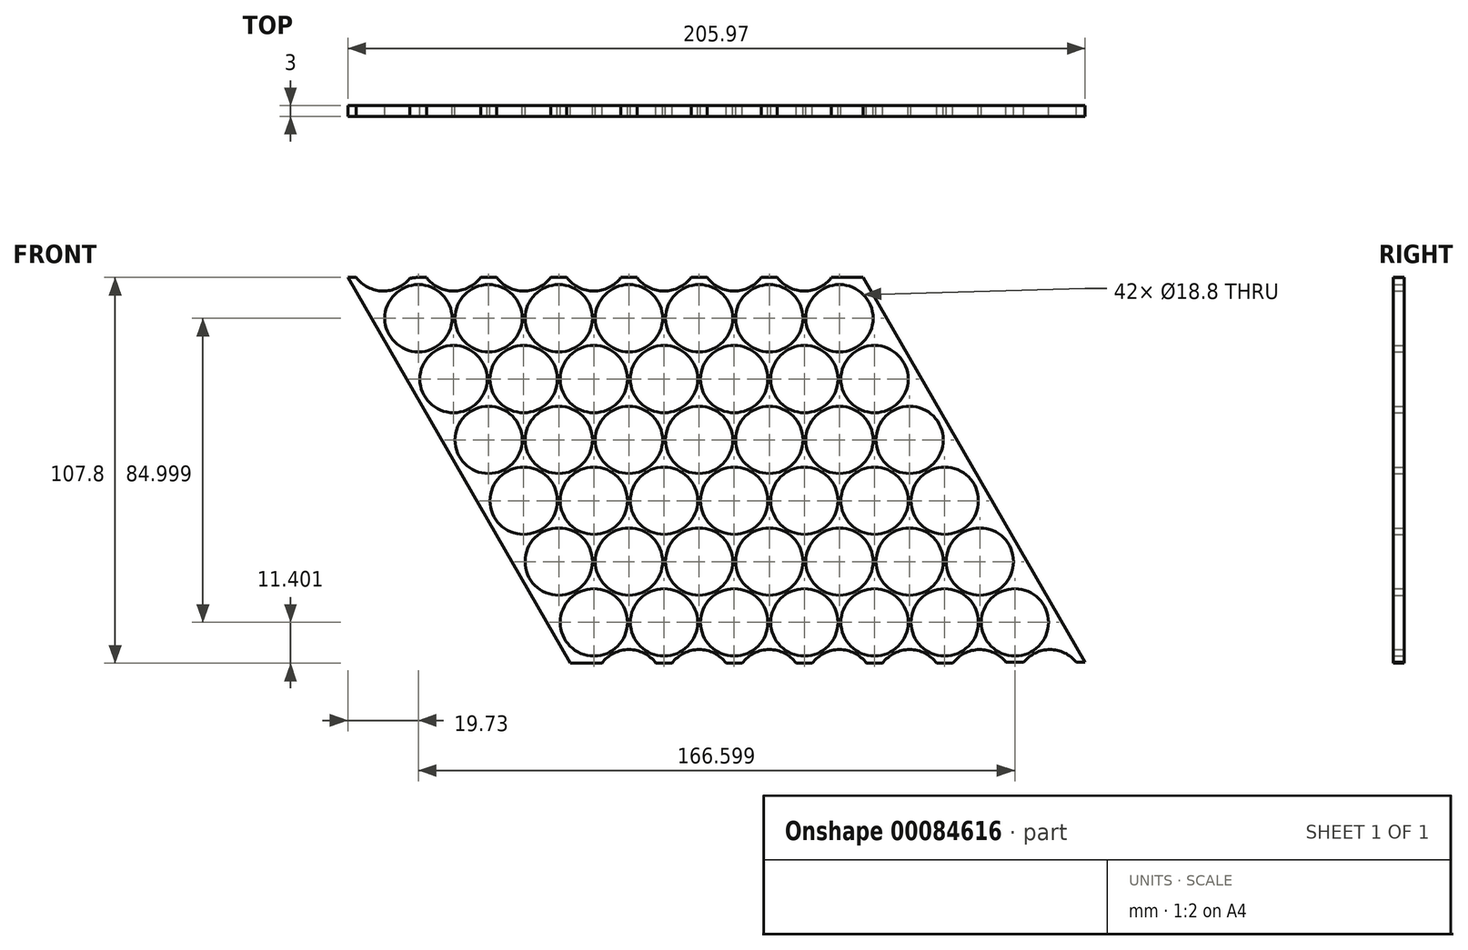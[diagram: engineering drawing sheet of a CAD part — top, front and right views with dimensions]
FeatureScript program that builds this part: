
annotation { "Feature Type Name" : "Feature", "Feature Type Description" : "" }
export const myFeature = defineFeature(function(context is Context, id is Id, definition is map)
    precondition{}
    {
        {
            var Q0;
            Q0=qCreatedBy(makeId("Front.planeOp"),FACE);
            var sketch = newSketch(context, id + "F0", { "sketchPlane" : qUnion([Q0])});
            skCircle(sketch, "E0", {"center": v(0, 0) * mm, "radius": 9.4 * mm});
            skCircle(sketch, "E1.1.0.0", {"center": v(19.6, 0) * mm, "radius": 9.4 * mm});
            skCircle(sketch, "E1.2.0.0", {"center": v(39.2, 0) * mm, "radius": 9.4 * mm});
            skCircle(sketch, "E1.3.0.0", {"center": v(58.8, 0) * mm, "radius": 9.4 * mm});
            skLineSegment(sketch, "E1.direction1", {"start": v(0, 0) * mm, "end": v(19.6, 0) * mm, "construction": true});
            skLineSegment(sketch, "E2", {"start": v(0, -17) * mm, "end": v(73.2, -17) * mm, "construction": true});
            skLineSegment(sketch, "E3", {"start": v(9.8, 0) * mm, "end": v(9.8, -17) * mm, "construction": true});
            skCircle(sketch, "E4", {"center": v(9.8, -17) * mm, "radius": 9.4 * mm});
            skCircle(sketch, "E5.1.0.0", {"center": v(29.4, -17) * mm, "radius": 9.4 * mm});
            skCircle(sketch, "E5.2.0.0", {"center": v(49, -17) * mm, "radius": 9.4 * mm});
            skCircle(sketch, "E5.3.0.0", {"center": v(68.6, -17) * mm, "radius": 9.4 * mm});
            skLineSegment(sketch, "E5.direction1", {"start": v(9.8, -17) * mm, "end": v(29.4, -17) * mm, "construction": true});
            skLineSegment(sketch, "E6", {"start": v(9.8, -17) * mm, "end": v(9.8, -26.4) * mm, "construction": true});
            skLineSegment(sketch, "E7", {"start": v(68.6, -17) * mm, "end": v(68.6, -26.4) * mm, "construction": true});
            skArc(sketch, "E8", {"start": v(58.8, 9.4) * mm, "mid": v(63.5, 8.14) * mm, "end": v(66.94, 4.7) * mm});
            skArc(sketch, "E9", {"start": v(76.74, -12.3) * mm, "mid": v(76.74, -21.7) * mm, "end": v(68.6, -26.4) * mm});
            skArc(sketch, "E10", {"start": v(9.8, -26.4) * mm, "mid": v(5.1, -25.14) * mm, "end": v(1.66, -21.7) * mm});
            skArc(sketch, "E11", {"start": v(-8.14, -4.7) * mm, "mid": v(-8.14, 4.7) * mm, "end": v(0, 9.4) * mm});
            skArc(sketch, "E12.0", {"start": v(0, 11.4) * mm, "mid": v(-1.24, 11.33) * mm, "end": v(-2.46, 11.13) * mm});
            skLineSegment(sketch, "E13.0", {"start": v(0, 11.4) * mm, "end": v(2.25, 11.4) * mm});
            skLineSegment(sketch, "E14.0", {"start": v(-9.88, -5.7) * mm, "end": v(-0.08, -22.7) * mm});
            skArc(sketch, "E15.trimOffspring", {"start": v(9.8, -5.82) * mm, "mid": v(9.87, -5.71) * mm, "end": v(9.93, -5.6) * mm});
            skArc(sketch, "E16.trimOffspring", {"start": v(9.93, -5.6) * mm, "mid": v(9.86, -5.6) * mm, "end": v(9.8, -5.6) * mm});
            skCircle(sketch, "E17.0.4.0", {"center": v(78.4, 0) * mm, "radius": 9.4 * mm});
            skCircle(sketch, "E17.0.5.0", {"center": v(98, 0) * mm, "radius": 9.4 * mm});
            skCircle(sketch, "E18.0.4.0", {"center": v(88.2, -17) * mm, "radius": 9.4 * mm});
            skCircle(sketch, "E18.0.5.0", {"center": v(107.8, -17) * mm, "radius": 9.4 * mm});
            skLineSegment(sketch, "E19", {"start": v(58.8, 11.4) * mm, "end": v(61.05, 11.4) * mm});
            skLineSegment(sketch, "E20", {"start": v(0, 0) * mm, "end": v(9.8, -17) * mm, "construction": true});
            skCircle(sketch, "E21.1.0.0", {"center": v(19.6, -34) * mm, "radius": 9.4 * mm});
            skCircle(sketch, "E21.2.0.0", {"center": v(29.4, -51) * mm, "radius": 9.4 * mm});
            skLineSegment(sketch, "E21.direction1", {"start": v(9.8, -17) * mm, "end": v(19.6, -34) * mm, "construction": true});
            skCircle(sketch, "E22.1.0.0", {"center": v(39.2, -34) * mm, "radius": 9.4 * mm});
            skCircle(sketch, "E22.1.0.1", {"center": v(49, -51) * mm, "radius": 9.4 * mm});
            skCircle(sketch, "E22.2.0.0", {"center": v(58.8, -34) * mm, "radius": 9.4 * mm});
            skCircle(sketch, "E22.2.0.1", {"center": v(68.6, -51) * mm, "radius": 9.4 * mm});
            skCircle(sketch, "E22.3.0.0", {"center": v(78.4, -34) * mm, "radius": 9.4 * mm});
            skCircle(sketch, "E22.3.0.1", {"center": v(88.2, -51) * mm, "radius": 9.4 * mm});
            skCircle(sketch, "E22.4.0.0", {"center": v(98, -34) * mm, "radius": 9.4 * mm});
            skCircle(sketch, "E22.4.0.1", {"center": v(107.8, -51) * mm, "radius": 9.4 * mm});
            skCircle(sketch, "E22.5.0.0", {"center": v(117.6, -34) * mm, "radius": 9.4 * mm});
            skCircle(sketch, "E22.5.0.1", {"center": v(127.4, -51) * mm, "radius": 9.4 * mm});
            skLineSegment(sketch, "E22.direction1", {"start": v(19.6, -34) * mm, "end": v(39.2, -34) * mm, "construction": true});
            skLineSegment(sketch, "E23", {"start": v(-0.08, -22.7) * mm, "end": v(19.52, -56.7) * mm});
            skArc(sketch, "E24.0", {"start": v(29.27, -62.4) * mm, "mid": v(29.33, -62.4) * mm, "end": v(29.4, -62.4) * mm});
            skCircle(sketch, "E25.0.6.0", {"center": v(117.6, 0) * mm, "radius": 9.4 * mm});
            skCircle(sketch, "E26.0.6.0", {"center": v(127.4, -17) * mm, "radius": 9.4 * mm});
            skCircle(sketch, "E27.0.6.0", {"center": v(137.2, -34) * mm, "radius": 9.4 * mm});
            skCircle(sketch, "E27.2.6.0", {"center": v(147, -51) * mm, "radius": 9.4 * mm});
            skLineSegment(sketch, "E28", {"start": v(98, 11.4) * mm, "end": v(100.25, 11.4) * mm});
            skCircle(sketch, "E29.0.3.0", {"center": v(39.2, -68) * mm, "radius": 9.4 * mm});
            skCircle(sketch, "E30.1.0.0", {"center": v(58.8, -68) * mm, "radius": 9.4 * mm});
            skCircle(sketch, "E30.2.0.0", {"center": v(78.4, -68) * mm, "radius": 9.4 * mm});
            skCircle(sketch, "E30.3.0.0", {"center": v(98, -68) * mm, "radius": 9.4 * mm});
            skCircle(sketch, "E30.4.0.0", {"center": v(117.6, -68) * mm, "radius": 9.4 * mm});
            skCircle(sketch, "E30.5.0.0", {"center": v(137.2, -68) * mm, "radius": 9.4 * mm});
            skCircle(sketch, "E30.6.0.0", {"center": v(156.8, -68) * mm, "radius": 9.4 * mm});
            skLineSegment(sketch, "E30.direction1", {"start": v(39.2, -68) * mm, "end": v(58.8, -68) * mm, "construction": true});
            skArc(sketch, "E31.0", {"start": v(39.07, -79.4) * mm, "mid": v(39.13, -79.4) * mm, "end": v(39.2, -79.4) * mm});
            skLineSegment(sketch, "E32", {"start": v(19.52, -56.7) * mm, "end": v(29.32, -73.7) * mm});
            skLineSegment(sketch, "E33", {"start": v(127.48, 5.7) * mm, "end": v(166.68, -62.3) * mm});
            skCircle(sketch, "E34.0.4.0", {"center": v(49, -85) * mm, "radius": 9.4 * mm});
            skArc(sketch, "E34.0.5.0", {"start": v(66.35, -96.4) * mm, "mid": v(58.8, -92.6) * mm, "end": v(51.25, -96.4) * mm});
            skCircle(sketch, "E35.1.0.0", {"center": v(68.6, -85) * mm, "radius": 9.4 * mm});
            skArc(sketch, "E35.1.0.1", {"start": v(85.95, -96.4) * mm, "mid": v(78.4, -92.6) * mm, "end": v(70.85, -96.4) * mm});
            skCircle(sketch, "E35.2.0.0", {"center": v(88.2, -85) * mm, "radius": 9.4 * mm});
            skArc(sketch, "E35.2.0.1", {"start": v(105.55, -96.4) * mm, "mid": v(98, -92.6) * mm, "end": v(90.45, -96.4) * mm});
            skCircle(sketch, "E35.3.0.0", {"center": v(107.8, -85) * mm, "radius": 9.4 * mm});
            skArc(sketch, "E35.3.0.1", {"start": v(125.15, -96.4) * mm, "mid": v(117.6, -92.6) * mm, "end": v(110.05, -96.4) * mm});
            skCircle(sketch, "E35.4.0.0", {"center": v(127.4, -85) * mm, "radius": 9.4 * mm});
            skArc(sketch, "E35.4.0.1", {"start": v(144.75, -96.4) * mm, "mid": v(137.2, -92.6) * mm, "end": v(129.65, -96.4) * mm});
            skCircle(sketch, "E35.5.0.0", {"center": v(147, -85) * mm, "radius": 9.4 * mm});
            skArc(sketch, "E35.5.0.1", {"start": v(164.14, -96.13) * mm, "mid": v(156.63, -92.6) * mm, "end": v(149.25, -96.4) * mm});
            skCircle(sketch, "E35.6.0.0", {"center": v(166.6, -85) * mm, "radius": 9.4 * mm});
            skArc(sketch, "E35.6.0.1", {"start": v(175, -92.7) * mm, "mid": v(171.7, -93.85) * mm, "end": v(169.05, -96.13) * mm});
            skLineSegment(sketch, "E35.direction1", {"start": v(49, -85) * mm, "end": v(68.6, -85) * mm, "construction": true});
            skLineSegment(sketch, "E36", {"start": v(29.32, -73.7) * mm, "end": v(39.12, -90.7) * mm});
            skLineSegment(sketch, "E37", {"start": v(49, -96.4) * mm, "end": v(51.25, -96.4) * mm});
            skLineSegment(sketch, "E38.trimOffspring", {"start": v(66.35, -96.4) * mm, "end": v(70.85, -96.4) * mm});
            skLineSegment(sketch, "E39.trimOffspring", {"start": v(85.95, -96.4) * mm, "end": v(90.45, -96.4) * mm});
            skLineSegment(sketch, "E40.trimOffspring", {"start": v(105.55, -96.4) * mm, "end": v(110.05, -96.4) * mm});
            skLineSegment(sketch, "E41.trimOffspring", {"start": v(125.15, -96.4) * mm, "end": v(129.65, -96.4) * mm});
            skLineSegment(sketch, "E42.trimOffspring", {"start": v(144.75, -96.4) * mm, "end": v(149.25, -96.4) * mm});
            skLineSegment(sketch, "E43.trimOffspring", {"start": v(156.67, -79.4) * mm, "end": v(156.8, -79.4) * mm});
            skLineSegment(sketch, "E44", {"start": v(164.14, -96.13) * mm, "end": v(169.05, -96.13) * mm});
            skLineSegment(sketch, "E45", {"start": v(166.68, -62.3) * mm, "end": v(176.48, -79.3) * mm});
            skArc(sketch, "E46.trimOffspring", {"start": v(48.87, -96.4) * mm, "mid": v(48.93, -96.4) * mm, "end": v(49, -96.4) * mm});
            skArc(sketch, "E47.1.0.0", {"start": v(-8.4, 7.7) * mm, "mid": v(-5.1, 8.86) * mm, "end": v(-2.46, 11.13) * mm});
            skLineSegment(sketch, "E47.1.0.1", {"start": v(-9.8, 17) * mm, "end": v(0, 0) * mm, "construction": true});
            skLineSegment(sketch, "E47.direction1", {"start": v(0, 0) * mm, "end": v(-9.8, 17) * mm, "construction": true});
            skArc(sketch, "E48.1.0.0", {"start": v(2.25, 11.4) * mm, "mid": v(9.8, 7.6) * mm, "end": v(17.35, 11.4) * mm});
            skArc(sketch, "E48.2.0.0", {"start": v(21.85, 11.4) * mm, "mid": v(29.4, 7.6) * mm, "end": v(36.95, 11.4) * mm});
            skArc(sketch, "E48.3.0.0", {"start": v(41.45, 11.4) * mm, "mid": v(49, 7.6) * mm, "end": v(56.55, 11.4) * mm});
            skArc(sketch, "E48.4.0.0", {"start": v(61.05, 11.4) * mm, "mid": v(68.6, 7.6) * mm, "end": v(76.15, 11.4) * mm});
            skArc(sketch, "E48.5.0.0", {"start": v(80.65, 11.4) * mm, "mid": v(88.2, 7.6) * mm, "end": v(95.75, 11.4) * mm});
            skArc(sketch, "E48.6.0.0", {"start": v(100.25, 11.4) * mm, "mid": v(107.8, 7.6) * mm, "end": v(115.35, 11.4) * mm});
            skLineSegment(sketch, "E48.direction1", {"start": v(-9.8, 17) * mm, "end": v(9.8, 17) * mm, "construction": true});
            skLineSegment(sketch, "E49.trimOffspring", {"start": v(115.35, 11.4) * mm, "end": v(117.6, 11.4) * mm});
            skLineSegment(sketch, "E50.trimOffspring", {"start": v(95.75, 11.4) * mm, "end": v(98, 11.4) * mm});
            skLineSegment(sketch, "E51.trimOffspring", {"start": v(76.15, 11.4) * mm, "end": v(80.65, 11.4) * mm});
            skLineSegment(sketch, "E52.trimOffspring", {"start": v(56.55, 11.4) * mm, "end": v(58.8, 11.4) * mm});
            skLineSegment(sketch, "E53.trimOffspring", {"start": v(36.95, 11.4) * mm, "end": v(41.45, 11.4) * mm});
            skLineSegment(sketch, "E54.trimOffspring", {"start": v(17.35, 11.4) * mm, "end": v(21.85, 11.4) * mm});
            skLineSegment(sketch, "E55", {"start": v(17.35, 11.4) * mm, "end": v(-33.98, 11.4) * mm, "construction": true});
            skLineSegment(sketch, "E56", {"start": v(-9.88, -5.7) * mm, "end": v(-19.73, 11.4) * mm});
            skArc(sketch, "E57", {"start": v(-17.35, 11.4) * mm, "mid": v(-9.97, 7.6) * mm, "end": v(-2.46, 11.13) * mm});
            skLineSegment(sketch, "E58", {"start": v(-19.73, 11.4) * mm, "end": v(-17.35, 11.4) * mm});
            skArc(sketch, "E59", {"start": v(183.74, -96.13) * mm, "mid": v(176.4, -92.6) * mm, "end": v(169.05, -96.13) * mm});
            skLineSegment(sketch, "E60", {"start": v(183.74, -96.13) * mm, "end": v(186.24, -96.13) * mm});
            skLineSegment(sketch, "E61", {"start": v(186.24, -96.13) * mm, "end": v(176.48, -79.3) * mm});
            skArc(sketch, "E62.trimOffspring", {"start": v(176.5, -79.34) * mm, "mid": v(176.48, -79.32) * mm, "end": v(176.48, -79.3) * mm});
            skArc(sketch, "E63", {"start": v(48.87, -96.4) * mm, "mid": v(48.87, -96.4) * mm, "end": v(48.87, -96.4) * mm});
            skLineSegment(sketch, "E64", {"start": v(39.12, -90.7) * mm, "end": v(42.41, -96.4) * mm});
            skLineSegment(sketch, "E65", {"start": v(51.25, -96.4) * mm, "end": v(42.41, -96.4) * mm});
            skLineSegment(sketch, "E66", {"start": v(127.48, 5.7) * mm, "end": v(124.19, 11.4) * mm});
            skLineSegment(sketch, "E67", {"start": v(117.6, 11.4) * mm, "end": v(124.19, 11.4) * mm});
            skSolve(sketch);
        }
        {
            var Q0;
            Q0=qSketchRegion(id+"F0",true);
            var Q1;
            {var subQ3=sQuery(id+"F0.wireOp",EDGE,"E1.1.0.0");Q1=makeQuery(id+"F0.imprint","IMPRINT",FACE,{"disambiguationData":[TD([[makeQuery(id+"F0.imprint","IMPRINT",EDGE,{"derivedFrom":subQ3}),-1.0]])]});}
            extrude(context, id + "F1", {"entities" : qUnion([Q0, Q1]), "depth" : 3 * mm});
        }
    });
